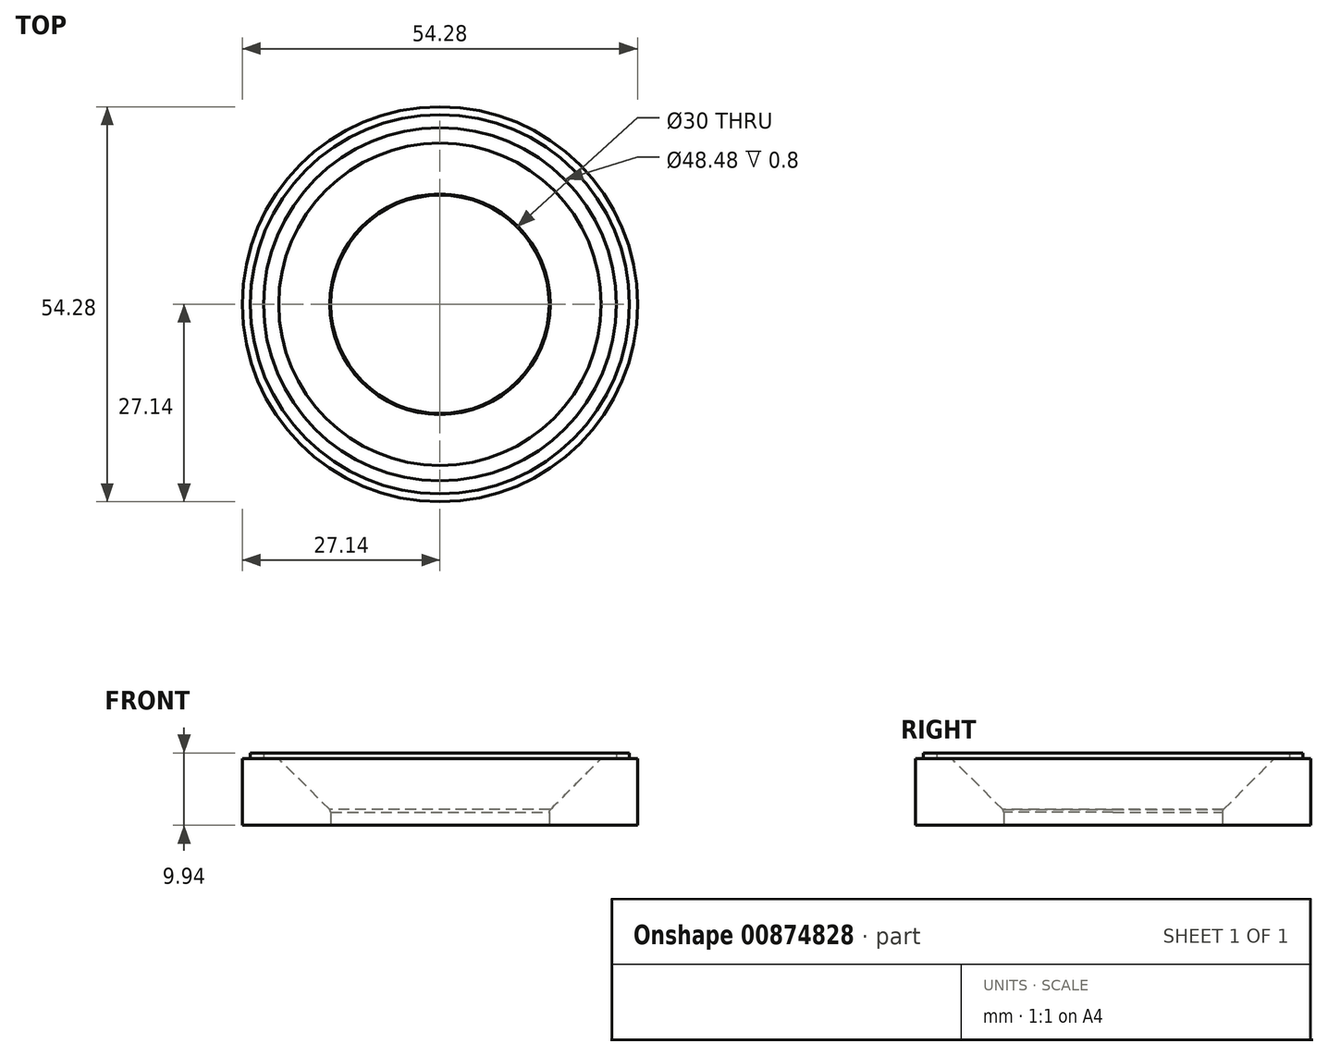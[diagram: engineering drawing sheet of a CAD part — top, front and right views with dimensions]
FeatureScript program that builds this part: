
annotation { "Feature Type Name" : "Feature", "Feature Type Description" : "" }
export const myFeature = defineFeature(function(context is Context, id is Id, definition is map)
    precondition{}
    {
        {
            var Q0;
            Q0=qCreatedBy(makeId("Front.planeOp"),FACE);
            var sketch = newSketch(context, id + "F0", { "sketchPlane" : qUnion([Q0])});
            skPoint(sketch, "E0.endSnap0", {"position": v(-14.28, 7.14) * mm});
            skLineSegment(sketch, "E1", {"start": v(0, 0) * mm, "end": v(-7.14, 7.14) * mm});
            skPoint(sketch, "E2.endSnap0", {"position": v(0, 7.14) * mm});
            skPoint(sketch, "E3.orphan", {"position": v(-14.28, 14.28) * mm});
            skPoint(sketch, "E4.right.start.orphan", {"position": v(-14.28, 0) * mm});
            skPoint(sketch, "E4.bottom.end.orphan", {"position": v(-7.14, 0) * mm});
            skLineSegment(sketch, "E5", {"start": v(0, 0) * mm, "end": v(0, -2) * mm});
            skLineSegment(sketch, "E6", {"start": v(-7.14, 7.14) * mm, "end": v(-12.14, 7.14) * mm});
            skLineSegment(sketch, "E7", {"start": v(0, -2) * mm, "end": v(-12.14, -2) * mm});
            skLineSegment(sketch, "E8", {"start": v(-12.14, -2) * mm, "end": v(-12.14, 7.14) * mm});
            skPoint(sketch, "E9.end.orphan", {"position": v(15, 7.14) * mm});
            skPoint(sketch, "E9.start.orphan", {"position": v(7.14, 7.14) * mm});
            skPoint(sketch, "E10.end.orphan", {"position": v(15, -2) * mm});
            skPoint(sketch, "E11.end.orphan", {"position": v(0, 14.28) * mm});
            skPoint(sketch, "E11.start.orphan", {"position": v(-9.64, 14.28) * mm});
            skLineSegment(sketch, "E12", {"start": v(15, -2) * mm, "end": v(15, 7.14) * mm});
            skLineSegment(sketch, "E13", {"start": v(-12.14, 7.14) * mm, "end": v(-11.04, 7.14) * mm});
            skLineSegment(sketch, "E14", {"start": v(-11.04, 7.14) * mm, "end": v(-9.24, 7.14) * mm});
            skLineSegment(sketch, "E15", {"start": v(-9.24, 7.14) * mm, "end": v(-7.14, 7.14) * mm});
            skLineSegment(sketch, "E16", {"start": v(-11.04, 7.94) * mm, "end": v(-11.04, 7.14) * mm});
            skLineSegment(sketch, "E17", {"start": v(-11.04, 7.94) * mm, "end": v(-9.24, 7.94) * mm});
            skLineSegment(sketch, "E18", {"start": v(-9.24, 7.14) * mm, "end": v(-9.24, 7.94) * mm});
            skSolve(sketch);
        }
        {
            var Q0;
            {var subQ0=sQuery(id+"F0.wireOp",EDGE,"E16");Q0=makeQuery(id+"F0.imprint","IMPRINT",FACE,{"disambiguationData":[TD([[makeQuery(id+"F0.imprint","IMPRINT",EDGE,{"derivedFrom":subQ0}),1.0]])]});}
            var Q1;
            {var subQ3=sQuery(id+"F0.wireOp",EDGE,"E1");Q1=makeQuery(id+"F0.imprint","IMPRINT",FACE,{"disambiguationData":[TD([[makeQuery(id+"F0.imprint","IMPRINT",EDGE,{"derivedFrom":subQ3}),1.0]])]});}
            var Q2;
            Q2=sQuery(id+"F0.wireOp",EDGE,"E12");
            revolve(context, id + "F1", {"surfaceOperationType" : NewSurfaceOperationType.NEW, "entities" : qUnion([Q0, Q1]), "axis" : qUnion([Q2]), "revolveType" : RevolveType.FULL});
        }
        {
            var Q0;
            Q0=makeQuery(id+"F1.opRevolve","SWEPT_EDGE",EDGE,{"disambiguationData":[OSD([sQuery(id+"F0.wireOp",EDGE,"E1"),sQuery(id+"F0.wireOp",EDGE,"E5")])]});
            chamfer(context, id + "F2", {"entities" : qUnion([Q0]), "width" : 0.5 * mm, "tangentPropagation" : true});
        }
    });
